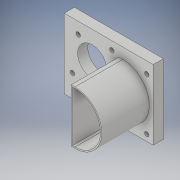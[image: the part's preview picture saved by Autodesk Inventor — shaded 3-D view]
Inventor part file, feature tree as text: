
AUTODESK INVENTOR PART (.ipt)
format: ipt  version: 2019 (Build 230136000, 136)  size: 173,568 bytes
history: native  units: mm
features: sketch x6, extrude x5, hole x1
ambient origin geometry x8: Origin, YZ Plane, XZ Plane, XY Plane, X Axis, Y Axis, Z Axis, Center Point
bodies: Solid1 (feature_tree)
feature tree (12):
  extrude  "Extrusion1"  Depth=55.0mm
  extrude  "Extrusion2"  Depth=8.0mm
  extrude  "Extrusion3"  Depth=3.5mm
  hole  "Hole1"  [1 undecoded]
  extrude  "Extrusion4"  Depth=9.0mm
  extrude  "Extrusion5"  Depth=40.0mm TaperAngle=0.0deg
  sketch  "Sketch1"  dims[d0=70.0mm d1=55.0mm]
  sketch  "Sketch2"  dims[d2=8.0mm d3=0.0mm d4=3.5mm]
  sketch  "Sketch3"  dims[d5=3.5mm d6=3.5mm]
  sketch  "Sketch4"  dims[d7=3.5mm d8=11.0mm]
  sketch  "Sketch5"  dims[d9=5.0mm d10=9.0mm]
  sketch  "Sketch6"  dims[d11=5.0mm d12=40.0mm d13=0.0mm d14=23.0mm d15=22.0mm d16=22.0mm d17=35.0mm d18=0.0mm d19=15.5mm d20=15.5mm d21=15.5mm d22=15.5mm d23=3.5mm d24=6.0mm d25=4.0mm d26=2.0mm d27=90.0deg d28=8.0mm d29=20.594885mm d30=40.0mm d32=25.5mm d33=24.0mm d34=26.0mm d35=35.0mm d36=0.0mm d37=42.0mm d38=27.0mm d39=37.5mm d40=0.0mm]
note: 1 required parameter value undecoded (feature->parameter linkage not recoverable at this tier; creation-order binding heuristic only, values carry confidence <= 0.55)
